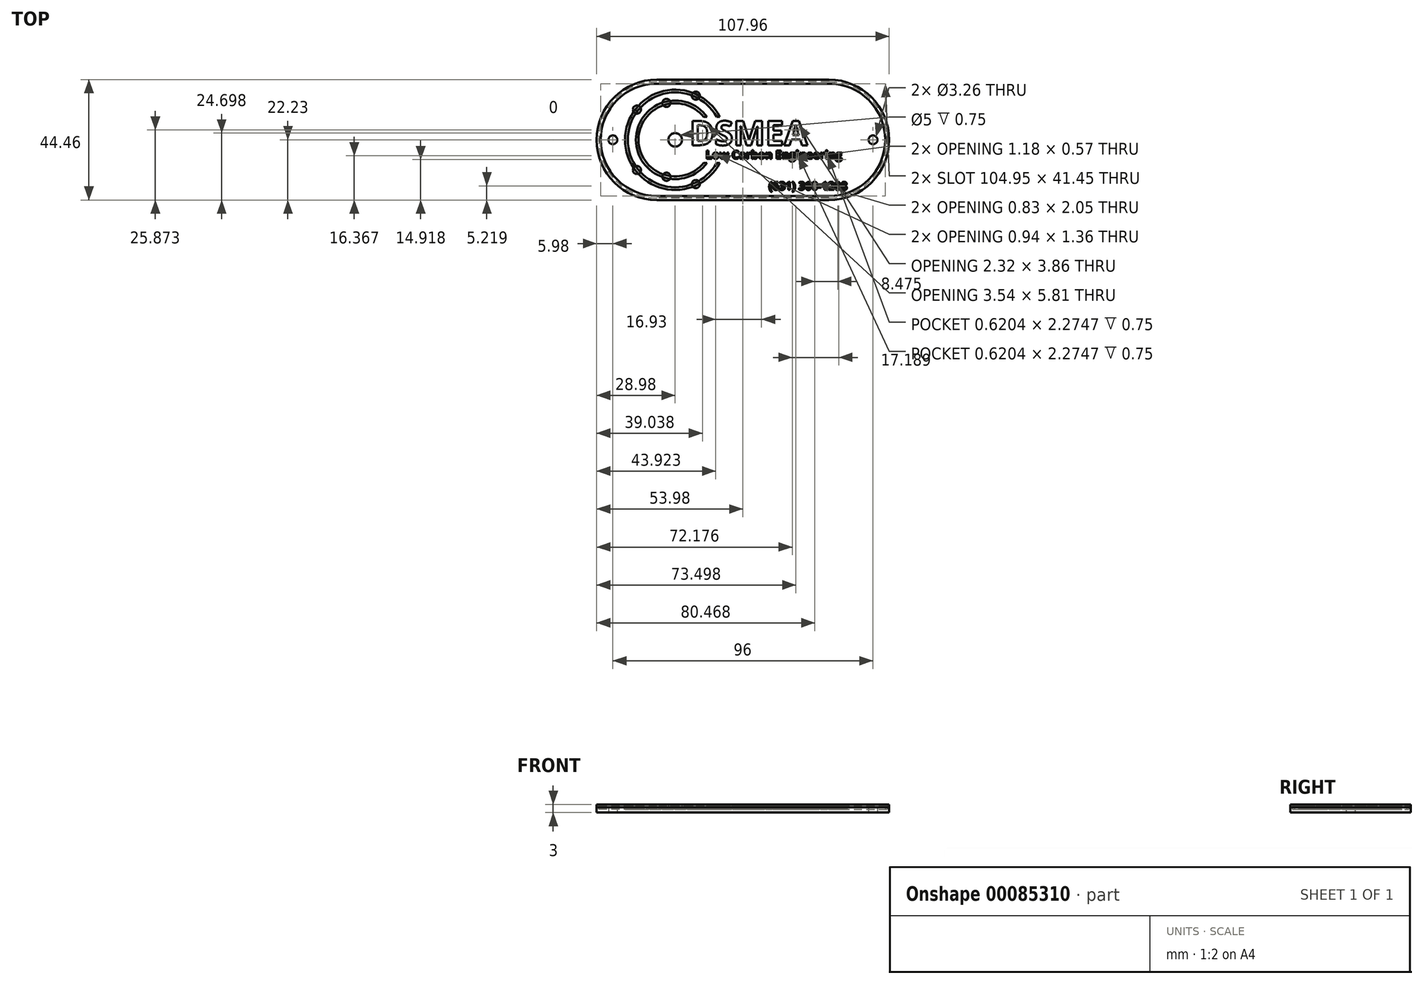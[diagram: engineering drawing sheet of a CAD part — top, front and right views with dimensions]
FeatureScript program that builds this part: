
annotation { "Feature Type Name" : "Feature", "Feature Type Description" : "" }
export const myFeature = defineFeature(function(context is Context, id is Id, definition is map)
    precondition{}
    {
        {
            var Q0;
            Q0=qCreatedBy(makeId("Top.planeOp"),FACE);
            var sketch = newSketch(context, id + "F0", { "sketchPlane" : qUnion([Q0])});
            skLineSegment(sketch, "E0.bottom", {"start": v(31.75, 22.22) * mm, "end": v(-31.75, 22.22) * mm});
            skLineSegment(sketch, "E0.top", {"start": v(31.75, -22.23) * mm, "end": v(-31.75, -22.23) * mm});
            skPoint(sketch, "E0.middle", {"position": v(0, 0) * mm});
            skArc(sketch, "E1", {"start": v(31.75, -22.23) * mm, "mid": v(53.98, 0) * mm, "end": v(31.75, 22.23) * mm});
            skArc(sketch, "E2", {"start": v(-31.75, 22.23) * mm, "mid": v(-53.98, 0) * mm, "end": v(-31.75, -22.23) * mm});
            skSolve(sketch);
        }
        {
            var Q0;
            Q0 = qSketchRegion(id + "F0", true);
            extrude(context, id + "F1", {"entities" : qUnion([Q0]), "depth" : 2 * mm});
        }
        {
            var Q0;
            Q0=qCreatedBy(makeId("Top.planeOp"),FACE);
            cPlane(context, id + "F2", {"entities" : qUnion([Q0]), "cplaneType" : CPlaneType.OFFSET, "offset" : 1.25 * mm, "width" : 150 * mm, "height" : 150 * mm});
        }
        {
            var Q0;
            Q0=qCreatedBy(id+"F2.planeOp",FACE);
            var sketch = newSketch(context, id + "F3", { "sketchPlane" : qUnion([Q0])});
            skPoint(sketch, "E3.middle", {"position": v(0, 0) * mm});
            skLineSegment(sketch, "E4.0", {"start": v(31.75, 20.73) * mm, "end": v(-31.75, 20.73) * mm});
            skArc(sketch, "E5.0", {"start": v(31.75, -20.73) * mm, "mid": v(52.48, 0) * mm, "end": v(31.75, 20.73) * mm});
            skLineSegment(sketch, "E6.0", {"start": v(31.75, -20.73) * mm, "end": v(-31.75, -20.73) * mm});
            skArc(sketch, "E7.0", {"start": v(-31.75, 20.73) * mm, "mid": v(-52.48, 0) * mm, "end": v(-31.75, -20.73) * mm});
            skLineSegment(sketch, "E8.0", {"start": v(31.75, 21.48) * mm, "end": v(-31.75, 21.48) * mm});
            skArc(sketch, "E9.0", {"start": v(-31.75, 21.48) * mm, "mid": v(-53.23, 0) * mm, "end": v(-31.75, -21.48) * mm});
            skArc(sketch, "E10.0", {"start": v(31.75, -21.48) * mm, "mid": v(53.23, 0) * mm, "end": v(31.75, 21.48) * mm});
            skLineSegment(sketch, "E11.0", {"start": v(31.75, -21.48) * mm, "end": v(-31.75, -21.48) * mm});
            skSolve(sketch);
        }
        {
            var Q0;
            Q0 = qSketchRegion(id + "F3", true);
            extrude(context, id + "F4", {"entities" : qUnion([Q0]), "depth" : 1.25 * mm});
        }
        {
            var Q0;
            {var subQ0=sQuery(id+"F0.wireOp",EDGE,"E0.bottom");var subQ1=makeQuery(id+"F1.opExtrude","SWEPT_FACE",FACE,{"disambiguationData":[OSD([subQ0])]});var subQ3=sQuery(id+"F0.wireOp",EDGE,"E0.top");var subQ5=sQuery(id+"F0.wireOp",EDGE,"E1");var subQ7=sQuery(id+"F0.wireOp",EDGE,"E2");Q0=makeQuery(id+"F14.boolean.opBoolean","SPLIT",FACE,{"disambiguationData":[TD([subQ1])],"derivedFrom":makeQuery(id+"F8.boolean.opBoolean","SPLIT",FACE,{"disambiguationData":[TD([subQ1])],"derivedFrom":makeQuery(id+"F1.opExtrude","CAP_FACE",FACE,{"disambiguationData":[OSD([subQ0,subQ3,subQ5,subQ7])],"isStart":false})})});}
            var sketch = newSketch(context, id + "F5", { "sketchPlane" : qUnion([Q0])});
            skArc(sketch, "E12", {"start": v(-31.75, 22.23) * mm, "mid": v(-53.98, 0) * mm, "end": v(-31.75, -22.23) * mm});
            skArc(sketch, "E13.0", {"start": v(-31.75, 20.73) * mm, "mid": v(-52.48, 0) * mm, "end": v(-31.75, -20.73) * mm});
            skArc(sketch, "E14.MirrorC", {"start": v(31.75, 22.23) * mm, "mid": v(53.98, 0) * mm, "end": v(31.75, -22.23) * mm});
            skArc(sketch, "E15.MirrorC", {"start": v(31.75, 20.73) * mm, "mid": v(52.48, 0) * mm, "end": v(31.75, -20.73) * mm});
            skLineSegment(sketch, "E16", {"start": v(-31.75, -22.23) * mm, "end": v(31.75, -22.23) * mm});
            skLineSegment(sketch, "E17.MirrorCS", {"start": v(-31.75, 22.23) * mm, "end": v(31.75, 22.23) * mm});
            skLineSegment(sketch, "E18.0", {"start": v(-31.75, 20.73) * mm, "end": v(31.75, 20.73) * mm});
            skLineSegment(sketch, "E19.MirrorCS", {"start": v(-31.75, -20.73) * mm, "end": v(31.75, -20.73) * mm});
            skSolve(sketch);
        }
        {
            var Q0;
            Q0 = qSketchRegion(id + "F5", true);
            extrude(context, id + "F6", {"entities" : qUnion([Q0]), "depth" : 1 * mm});
        }
        {
            var Q0;
            Q0=qCreatedBy(id+"F2.planeOp",FACE);
            var sketch = newSketch(context, id + "F7", { "sketchPlane" : qUnion([Q0])});
            skArc(sketch, "E20", {"start": v(-8.57, 8.5) * mm, "mid": v(-43.5, 0) * mm, "end": v(-8.57, -8.5) * mm});
            skArc(sketch, "E21", {"start": v(-9.7, 8.5) * mm, "mid": v(-42.5, 0) * mm, "end": v(-9.7, -8.5) * mm});
            skLineSegment(sketch, "E22.bottom", {"start": v(-8.57, 8.5) * mm, "end": v(-9.7, 8.5) * mm});
            skLineSegment(sketch, "E22.top", {"start": v(-8.57, -8.5) * mm, "end": v(-9.7, -8.5) * mm});
            skPoint(sketch, "E22.middle", {"position": v(0, 0) * mm});
            skSolve(sketch);
        }
        {
            var Q0;
            Q0 = qSketchRegion(id + "F7", true);
            extrude(context, id + "F8", {"entities" : qUnion([Q0]), "depth" : 1.75 * mm});
        }
        {
            var Q0;
            Q0=qCreatedBy(id+"F2.planeOp",FACE);
            var sketch = newSketch(context, id + "F9", { "sketchPlane" : qUnion([Q0])});
            skArc(sketch, "E23", {"start": v(-13.25, 8.5) * mm, "mid": v(-39.5, 0) * mm, "end": v(-13.25, -8.5) * mm});
            skArc(sketch, "E24", {"start": v(-14.51, 8.5) * mm, "mid": v(-38.5, 0) * mm, "end": v(-14.51, -8.5) * mm});
            skLineSegment(sketch, "E25.bottom", {"start": v(-13.25, 8.5) * mm, "end": v(-14.51, 8.5) * mm});
            skLineSegment(sketch, "E25.top", {"start": v(-13.25, -8.5) * mm, "end": v(-14.51, -8.5) * mm});
            skPoint(sketch, "E25.middle", {"position": v(0, 0) * mm});
            skSolve(sketch);
        }
        {
            var Q0;
            Q0 = qSketchRegion(id + "F9", true);
            extrude(context, id + "F10", {"entities" : qUnion([Q0]), "depth" : 1.75 * mm});
        }
        {
            var Q0;
            Q0=qCreatedBy(id+"F2.planeOp",FACE);
            var sketch = newSketch(context, id + "F11", { "sketchPlane" : qUnion([Q0])});
            skCircle(sketch, "E26", {"center": v(-25, 0) * mm, "radius": 2.5 * mm});
            skCircle(sketch, "E27", {"center": v(-17.4, 16.31) * mm, "radius": 1.5 * mm});
            skLineSegment(sketch, "E28.anchor1", {"start": v(-25, 0) * mm, "end": v(-17.4, 16.31) * mm, "construction": true});
            skLineSegment(sketch, "E28.anchor2", {"start": v(-25, 0) * mm, "end": v(-17.4, -16.31) * mm, "construction": true});
            skCircle(sketch, "E29", {"center": v(-28.23, 13.62) * mm, "radius": 1.5 * mm});
            skCircle(sketch, "E30.MirrorC", {"center": v(-28.23, -13.62) * mm, "radius": 1.5 * mm});
            skLineSegment(sketch, "E31", {"start": v(-59.58, 0) * mm, "end": v(0, 0) * mm, "construction": true});
            skCircle(sketch, "E32", {"center": v(-25, 0) * mm, "radius": 18 * mm, "construction": true});
            skCircle(sketch, "E33", {"center": v(-25, 0) * mm, "radius": 14 * mm, "construction": true});
            skLineSegment(sketch, "E34", {"start": v(-28.23, 13.62) * mm, "end": v(-35.98, 8.68) * mm, "construction": true});
            skLineSegment(sketch, "E35", {"start": v(-28.23, 13.62) * mm, "end": v(-19.08, 12.69) * mm, "construction": true});
            skCircle(sketch, "E36.1.0", {"center": v(-39.12, 11.16) * mm, "radius": 1.5 * mm});
            skCircle(sketch, "E36.2.0", {"center": v(-39.12, -11.16) * mm, "radius": 1.5 * mm});
            skCircle(sketch, "E36.3.0", {"center": v(-17.4, -16.31) * mm, "radius": 1.5 * mm});
            skSolve(sketch);
        }
        {
            var Q0;
            Q0 = qSketchRegion(id + "F11", true);
            extrude(context, id + "F12", {"entities" : qUnion([Q0]), "depth" : 1.75 * mm});
        }
        {
            var Q0;
            Q0=qCreatedBy(id+"F2.planeOp",FACE);
            var sketch = newSketch(context, id + "F13", { "sketchPlane" : qUnion([Q0])});
            skText(sketch, "E37", { "text": "DSMEA", "fontName": "OpenSans-Bold.ttf"});
            const initialGuessF13  = {"E37": [-0.01973, -0.002, 1, 0, 0.009]};
            skSetInitialGuess(sketch, initialGuessF13);
            skSolve(sketch);
        }
        {
            var Q0;
            Q0 = qSketchRegion(id + "F13", true);
            extrude(context, id + "F14", {"entities" : qUnion([Q0]), "depth" : 1.75 * mm});
        }
        {
            var Q0;
            Q0=qCreatedBy(id+"F2.planeOp",FACE);
            var sketch = newSketch(context, id + "F15", { "sketchPlane" : qUnion([Q0])});
            skText(sketch, "E38", { "text": "Low Carbon Engineering", "fontName": "OpenSans-Bold.ttf"});
            const initialGuessF15  = {"E38": [-0.0137, -0.007, 1, 0, 0.003]};
            skSetInitialGuess(sketch, initialGuessF15);
            skSolve(sketch);
        }
        {
            var Q0;
            Q0 = qSketchRegion(id + "F15", true);
            extrude(context, id + "F16", {"entities" : qUnion([Q0]), "depth" : 1.75 * mm});
        }
        {
            var Q0;
            Q0=qCreatedBy(id+"F2.planeOp",FACE);
            var sketch = newSketch(context, id + "F17", { "sketchPlane" : qUnion([Q0])});
            skText(sketch, "E39", { "text": "(631) 360-1208", "fontName": "OpenSans-Bold.ttf"});
            const initialGuessF17  = {"E39": [0.0095, -0.0185, 1, 0, 0.003]};
            skSetInitialGuess(sketch, initialGuessF17);
            skSolve(sketch);
        }
        {
            var Q0;
            Q0 = qSketchRegion(id + "F17", true);
            extrude(context, id + "F18", {"entities" : qUnion([Q0]), "depth" : 1.75 * mm});
        }
        {
            var Q0;
            Q0=makeQuery(id+"F4.opExtrude","SWEPT_BODY",BODY,{"disambiguationData":[OSD([sQuery(id+"F3.wireOp",EDGE,"E4.0"),sQuery(id+"F3.wireOp",EDGE,"E5.0"),sQuery(id+"F3.wireOp",EDGE,"E6.0"),sQuery(id+"F3.wireOp",EDGE,"E7.0"),sQuery(id+"F3.wireOp",EDGE,"E8.0"),sQuery(id+"F3.wireOp",EDGE,"E9.0"),sQuery(id+"F3.wireOp",EDGE,"E10.0"),sQuery(id+"F3.wireOp",EDGE,"E11.0")])]});
            var Q1;
            Q1=makeQuery(id+"F1.opExtrude","SWEPT_BODY",BODY,{"disambiguationData":[OSD([sQuery(id+"F0.wireOp",EDGE,"E0.bottom"),sQuery(id+"F0.wireOp",EDGE,"E0.top"),sQuery(id+"F0.wireOp",EDGE,"E1"),sQuery(id+"F0.wireOp",EDGE,"E2")])]});
            booleanBodies(context, id + "F19", {"operationType" : BooleanOperationType.SUBTRACTION, "tools" : qUnion([Q0]), "targets" : qUnion([Q1]), "keepTools" : true});
        }
        {
            var Q0;
            Q0=makeQuery(id+"F8.opExtrude","SWEPT_BODY",BODY,{"disambiguationData":[OSD([sQuery(id+"F7.wireOp",EDGE,"E20"),sQuery(id+"F7.wireOp",EDGE,"E21")])]});
            var Q1;
            Q1=makeQuery(id+"F1.opExtrude","SWEPT_BODY",BODY,{"disambiguationData":[OSD([sQuery(id+"F0.wireOp",EDGE,"E0.bottom"),sQuery(id+"F0.wireOp",EDGE,"E0.top"),sQuery(id+"F0.wireOp",EDGE,"E1"),sQuery(id+"F0.wireOp",EDGE,"E2")])]});
            booleanBodies(context, id + "F20", {"operationType" : BooleanOperationType.SUBTRACTION, "tools" : qUnion([Q0]), "targets" : qUnion([Q1]), "keepTools" : true});
        }
        {
            var Q0;
            Q0=makeQuery(id+"F8.opExtrude","SWEPT_BODY",BODY,{"disambiguationData":[OSD([sQuery(id+"F7.wireOp",EDGE,"E20"),sQuery(id+"F7.wireOp",EDGE,"E21")])]});
            var Q1;
            Q1=makeQuery(id+"F12.opExtrude","SWEPT_BODY",BODY,{"disambiguationData":[OSD([sQuery(id+"F11.wireOp",EDGE,"E26")])]});
            var Q2;
            Q2=makeQuery(id+"F10.opExtrude","SWEPT_BODY",BODY,{"disambiguationData":[OSD([sQuery(id+"F9.wireOp",EDGE,"E23"),sQuery(id+"F9.wireOp",EDGE,"E24")])]});
            var Q3;
            Q3=makeQuery(id+"F1.opExtrude","SWEPT_BODY",BODY,{"disambiguationData":[OSD([sQuery(id+"F0.wireOp",EDGE,"E0.bottom"),sQuery(id+"F0.wireOp",EDGE,"E0.top"),sQuery(id+"F0.wireOp",EDGE,"E1"),sQuery(id+"F0.wireOp",EDGE,"E2")])]});
            booleanBodies(context, id + "F21", {"operationType" : BooleanOperationType.SUBTRACTION, "tools" : qUnion([Q0, Q1, Q2]), "targets" : qUnion([Q3]), "keepTools" : true});
        }
        {
            var Q0;
            Q0=makeQuery(id+"F14.opExtrude","SWEPT_BODY",BODY,{"disambiguationData":[OSD([sQuery(id+"F13.wireOp",EDGE,"E37.sketch_text.stroke-0"),sQuery(id+"F13.wireOp",EDGE,"E37.sketch_text.stroke-1"),sQuery(id+"F13.wireOp",EDGE,"E37.sketch_text.stroke-2"),sQuery(id+"F13.wireOp",EDGE,"E37.sketch_text.stroke-3"),sQuery(id+"F13.wireOp",EDGE,"E37.sketch_text.stroke-4"),sQuery(id+"F13.wireOp",EDGE,"E37.sketch_text.stroke-5"),sQuery(id+"F13.wireOp",EDGE,"E37.sketch_text.stroke-6"),sQuery(id+"F13.wireOp",EDGE,"E37.sketch_text.stroke-7"),sQuery(id+"F13.wireOp",EDGE,"E37.sketch_text.stroke-8"),sQuery(id+"F13.wireOp",EDGE,"E37.sketch_text.stroke-9"),sQuery(id+"F13.wireOp",EDGE,"E37.sketch_text.stroke-10"),sQuery(id+"F13.wireOp",EDGE,"E37.sketch_text.stroke-11")])]});
            var Q1;
            Q1=makeQuery(id+"F14.opExtrude","SWEPT_BODY",BODY,{"disambiguationData":[OSD([sQuery(id+"F13.wireOp",EDGE,"E37.sketch_text.stroke-12"),sQuery(id+"F13.wireOp",EDGE,"E37.sketch_text.stroke-13"),sQuery(id+"F13.wireOp",EDGE,"E37.sketch_text.stroke-14"),sQuery(id+"F13.wireOp",EDGE,"E37.sketch_text.stroke-15"),sQuery(id+"F13.wireOp",EDGE,"E37.sketch_text.stroke-16"),sQuery(id+"F13.wireOp",EDGE,"E37.sketch_text.stroke-17"),sQuery(id+"F13.wireOp",EDGE,"E37.sketch_text.stroke-18"),sQuery(id+"F13.wireOp",EDGE,"E37.sketch_text.stroke-19"),sQuery(id+"F13.wireOp",EDGE,"E37.sketch_text.stroke-20"),sQuery(id+"F13.wireOp",EDGE,"E37.sketch_text.stroke-21"),sQuery(id+"F13.wireOp",EDGE,"E37.sketch_text.stroke-22"),sQuery(id+"F13.wireOp",EDGE,"E37.sketch_text.stroke-23"),sQuery(id+"F13.wireOp",EDGE,"E37.sketch_text.stroke-24"),sQuery(id+"F13.wireOp",EDGE,"E37.sketch_text.stroke-25"),sQuery(id+"F13.wireOp",EDGE,"E37.sketch_text.stroke-26"),sQuery(id+"F13.wireOp",EDGE,"E37.sketch_text.stroke-27"),sQuery(id+"F13.wireOp",EDGE,"E37.sketch_text.stroke-28"),sQuery(id+"F13.wireOp",EDGE,"E37.sketch_text.stroke-29"),sQuery(id+"F13.wireOp",EDGE,"E37.sketch_text.stroke-30"),sQuery(id+"F13.wireOp",EDGE,"E37.sketch_text.stroke-31"),sQuery(id+"F13.wireOp",EDGE,"E37.sketch_text.stroke-32"),sQuery(id+"F13.wireOp",EDGE,"E37.sketch_text.stroke-33"),sQuery(id+"F13.wireOp",EDGE,"E37.sketch_text.stroke-34"),sQuery(id+"F13.wireOp",EDGE,"E37.sketch_text.stroke-35"),sQuery(id+"F13.wireOp",EDGE,"E37.sketch_text.stroke-36"),sQuery(id+"F13.wireOp",EDGE,"E37.sketch_text.stroke-37"),sQuery(id+"F13.wireOp",EDGE,"E37.sketch_text.stroke-38"),sQuery(id+"F13.wireOp",EDGE,"E37.sketch_text.stroke-39")])]});
            var Q2;
            Q2=makeQuery(id+"F14.opExtrude","SWEPT_BODY",BODY,{"disambiguationData":[OSD([sQuery(id+"F13.wireOp",EDGE,"E37.sketch_text.stroke-40"),sQuery(id+"F13.wireOp",EDGE,"E37.sketch_text.stroke-41"),sQuery(id+"F13.wireOp",EDGE,"E37.sketch_text.stroke-42"),sQuery(id+"F13.wireOp",EDGE,"E37.sketch_text.stroke-43"),sQuery(id+"F13.wireOp",EDGE,"E37.sketch_text.stroke-44"),sQuery(id+"F13.wireOp",EDGE,"E37.sketch_text.stroke-45"),sQuery(id+"F13.wireOp",EDGE,"E37.sketch_text.stroke-46"),sQuery(id+"F13.wireOp",EDGE,"E37.sketch_text.stroke-47"),sQuery(id+"F13.wireOp",EDGE,"E37.sketch_text.stroke-48"),sQuery(id+"F13.wireOp",EDGE,"E37.sketch_text.stroke-49"),sQuery(id+"F13.wireOp",EDGE,"E37.sketch_text.stroke-50"),sQuery(id+"F13.wireOp",EDGE,"E37.sketch_text.stroke-51"),sQuery(id+"F13.wireOp",EDGE,"E37.sketch_text.stroke-52"),sQuery(id+"F13.wireOp",EDGE,"E37.sketch_text.stroke-53"),sQuery(id+"F13.wireOp",EDGE,"E37.sketch_text.stroke-54"),sQuery(id+"F13.wireOp",EDGE,"E37.sketch_text.stroke-55"),sQuery(id+"F13.wireOp",EDGE,"E37.sketch_text.stroke-56"),sQuery(id+"F13.wireOp",EDGE,"E37.sketch_text.stroke-57"),sQuery(id+"F13.wireOp",EDGE,"E37.sketch_text.stroke-58")])]});
            var Q3;
            Q3=makeQuery(id+"F14.opExtrude","SWEPT_BODY",BODY,{"disambiguationData":[OSD([sQuery(id+"F13.wireOp",EDGE,"E37.sketch_text.stroke-59"),sQuery(id+"F13.wireOp",EDGE,"E37.sketch_text.stroke-60"),sQuery(id+"F13.wireOp",EDGE,"E37.sketch_text.stroke-61"),sQuery(id+"F13.wireOp",EDGE,"E37.sketch_text.stroke-62"),sQuery(id+"F13.wireOp",EDGE,"E37.sketch_text.stroke-63"),sQuery(id+"F13.wireOp",EDGE,"E37.sketch_text.stroke-64"),sQuery(id+"F13.wireOp",EDGE,"E37.sketch_text.stroke-65"),sQuery(id+"F13.wireOp",EDGE,"E37.sketch_text.stroke-66"),sQuery(id+"F13.wireOp",EDGE,"E37.sketch_text.stroke-67"),sQuery(id+"F13.wireOp",EDGE,"E37.sketch_text.stroke-68"),sQuery(id+"F13.wireOp",EDGE,"E37.sketch_text.stroke-69"),sQuery(id+"F13.wireOp",EDGE,"E37.sketch_text.stroke-70")])]});
            var Q4;
            Q4=makeQuery(id+"F14.opExtrude","SWEPT_BODY",BODY,{"disambiguationData":[OSD([sQuery(id+"F13.wireOp",EDGE,"E37.sketch_text.stroke-71"),sQuery(id+"F13.wireOp",EDGE,"E37.sketch_text.stroke-72"),sQuery(id+"F13.wireOp",EDGE,"E37.sketch_text.stroke-73"),sQuery(id+"F13.wireOp",EDGE,"E37.sketch_text.stroke-74"),sQuery(id+"F13.wireOp",EDGE,"E37.sketch_text.stroke-75"),sQuery(id+"F13.wireOp",EDGE,"E37.sketch_text.stroke-76"),sQuery(id+"F13.wireOp",EDGE,"E37.sketch_text.stroke-77"),sQuery(id+"F13.wireOp",EDGE,"E37.sketch_text.stroke-78"),sQuery(id+"F13.wireOp",EDGE,"E37.sketch_text.stroke-79"),sQuery(id+"F13.wireOp",EDGE,"E37.sketch_text.stroke-80"),sQuery(id+"F13.wireOp",EDGE,"E37.sketch_text.stroke-81"),sQuery(id+"F13.wireOp",EDGE,"E37.sketch_text.stroke-82")])]});
            var Q5;
            Q5=makeQuery(id+"F1.opExtrude","SWEPT_BODY",BODY,{"disambiguationData":[OSD([sQuery(id+"F0.wireOp",EDGE,"E0.bottom"),sQuery(id+"F0.wireOp",EDGE,"E0.top"),sQuery(id+"F0.wireOp",EDGE,"E1"),sQuery(id+"F0.wireOp",EDGE,"E2")])]});
            booleanBodies(context, id + "F22", {"operationType" : BooleanOperationType.SUBTRACTION, "tools" : qUnion([Q0, Q1, Q2, Q3, Q4]), "targets" : qUnion([Q5]), "keepTools" : true});
        }
        {
            var Q0;
            Q0=makeQuery(id+"F16.opExtrude","SWEPT_BODY",BODY,{"disambiguationData":[OSD([sQuery(id+"F15.wireOp",EDGE,"E38.sketch_text.stroke-0"),sQuery(id+"F15.wireOp",EDGE,"E38.sketch_text.stroke-1"),sQuery(id+"F15.wireOp",EDGE,"E38.sketch_text.stroke-2"),sQuery(id+"F15.wireOp",EDGE,"E38.sketch_text.stroke-3"),sQuery(id+"F15.wireOp",EDGE,"E38.sketch_text.stroke-4"),sQuery(id+"F15.wireOp",EDGE,"E38.sketch_text.stroke-5")])]});
            var Q1;
            Q1=makeQuery(id+"F16.opExtrude","SWEPT_BODY",BODY,{"disambiguationData":[OSD([sQuery(id+"F15.wireOp",EDGE,"E38.sketch_text.stroke-6"),sQuery(id+"F15.wireOp",EDGE,"E38.sketch_text.stroke-7"),sQuery(id+"F15.wireOp",EDGE,"E38.sketch_text.stroke-8"),sQuery(id+"F15.wireOp",EDGE,"E38.sketch_text.stroke-9"),sQuery(id+"F15.wireOp",EDGE,"E38.sketch_text.stroke-10"),sQuery(id+"F15.wireOp",EDGE,"E38.sketch_text.stroke-11"),sQuery(id+"F15.wireOp",EDGE,"E38.sketch_text.stroke-12"),sQuery(id+"F15.wireOp",EDGE,"E38.sketch_text.stroke-13"),sQuery(id+"F15.wireOp",EDGE,"E38.sketch_text.stroke-14"),sQuery(id+"F15.wireOp",EDGE,"E38.sketch_text.stroke-15"),sQuery(id+"F15.wireOp",EDGE,"E38.sketch_text.stroke-16"),sQuery(id+"F15.wireOp",EDGE,"E38.sketch_text.stroke-17"),sQuery(id+"F15.wireOp",EDGE,"E38.sketch_text.stroke-18"),sQuery(id+"F15.wireOp",EDGE,"E38.sketch_text.stroke-19"),sQuery(id+"F15.wireOp",EDGE,"E38.sketch_text.stroke-20"),sQuery(id+"F15.wireOp",EDGE,"E38.sketch_text.stroke-21"),sQuery(id+"F15.wireOp",EDGE,"E38.sketch_text.stroke-22"),sQuery(id+"F15.wireOp",EDGE,"E38.sketch_text.stroke-23")])]});
            var Q2;
            Q2=makeQuery(id+"F16.opExtrude","SWEPT_BODY",BODY,{"disambiguationData":[OSD([sQuery(id+"F15.wireOp",EDGE,"E38.sketch_text.stroke-24"),sQuery(id+"F15.wireOp",EDGE,"E38.sketch_text.stroke-25"),sQuery(id+"F15.wireOp",EDGE,"E38.sketch_text.stroke-26"),sQuery(id+"F15.wireOp",EDGE,"E38.sketch_text.stroke-27"),sQuery(id+"F15.wireOp",EDGE,"E38.sketch_text.stroke-28"),sQuery(id+"F15.wireOp",EDGE,"E38.sketch_text.stroke-29"),sQuery(id+"F15.wireOp",EDGE,"E38.sketch_text.stroke-30"),sQuery(id+"F15.wireOp",EDGE,"E38.sketch_text.stroke-31"),sQuery(id+"F15.wireOp",EDGE,"E38.sketch_text.stroke-32"),sQuery(id+"F15.wireOp",EDGE,"E38.sketch_text.stroke-33"),sQuery(id+"F15.wireOp",EDGE,"E38.sketch_text.stroke-34"),sQuery(id+"F15.wireOp",EDGE,"E38.sketch_text.stroke-35"),sQuery(id+"F15.wireOp",EDGE,"E38.sketch_text.stroke-36"),sQuery(id+"F15.wireOp",EDGE,"E38.sketch_text.stroke-37"),sQuery(id+"F15.wireOp",EDGE,"E38.sketch_text.stroke-38"),sQuery(id+"F15.wireOp",EDGE,"E38.sketch_text.stroke-39"),sQuery(id+"F15.wireOp",EDGE,"E38.sketch_text.stroke-40"),sQuery(id+"F15.wireOp",EDGE,"E38.sketch_text.stroke-41"),sQuery(id+"F15.wireOp",EDGE,"E38.sketch_text.stroke-42"),sQuery(id+"F15.wireOp",EDGE,"E38.sketch_text.stroke-43"),sQuery(id+"F15.wireOp",EDGE,"E38.sketch_text.stroke-44"),sQuery(id+"F15.wireOp",EDGE,"E38.sketch_text.stroke-45"),sQuery(id+"F15.wireOp",EDGE,"E38.sketch_text.stroke-46"),sQuery(id+"F15.wireOp",EDGE,"E38.sketch_text.stroke-47"),sQuery(id+"F15.wireOp",EDGE,"E38.sketch_text.stroke-48"),sQuery(id+"F15.wireOp",EDGE,"E38.sketch_text.stroke-49")])]});
            var Q3;
            Q3=makeQuery(id+"F16.opExtrude","SWEPT_BODY",BODY,{"disambiguationData":[OSD([sQuery(id+"F15.wireOp",EDGE,"E38.sketch_text.stroke-50"),sQuery(id+"F15.wireOp",EDGE,"E38.sketch_text.stroke-51"),sQuery(id+"F15.wireOp",EDGE,"E38.sketch_text.stroke-52"),sQuery(id+"F15.wireOp",EDGE,"E38.sketch_text.stroke-53"),sQuery(id+"F15.wireOp",EDGE,"E38.sketch_text.stroke-54"),sQuery(id+"F15.wireOp",EDGE,"E38.sketch_text.stroke-55"),sQuery(id+"F15.wireOp",EDGE,"E38.sketch_text.stroke-56"),sQuery(id+"F15.wireOp",EDGE,"E38.sketch_text.stroke-57"),sQuery(id+"F15.wireOp",EDGE,"E38.sketch_text.stroke-58"),sQuery(id+"F15.wireOp",EDGE,"E38.sketch_text.stroke-59"),sQuery(id+"F15.wireOp",EDGE,"E38.sketch_text.stroke-60"),sQuery(id+"F15.wireOp",EDGE,"E38.sketch_text.stroke-61"),sQuery(id+"F15.wireOp",EDGE,"E38.sketch_text.stroke-62"),sQuery(id+"F15.wireOp",EDGE,"E38.sketch_text.stroke-63"),sQuery(id+"F15.wireOp",EDGE,"E38.sketch_text.stroke-64")])]});
            var Q4;
            Q4=makeQuery(id+"F16.opExtrude","SWEPT_BODY",BODY,{"disambiguationData":[OSD([sQuery(id+"F15.wireOp",EDGE,"E38.sketch_text.stroke-65"),sQuery(id+"F15.wireOp",EDGE,"E38.sketch_text.stroke-66"),sQuery(id+"F15.wireOp",EDGE,"E38.sketch_text.stroke-67"),sQuery(id+"F15.wireOp",EDGE,"E38.sketch_text.stroke-68"),sQuery(id+"F15.wireOp",EDGE,"E38.sketch_text.stroke-69"),sQuery(id+"F15.wireOp",EDGE,"E38.sketch_text.stroke-70"),sQuery(id+"F15.wireOp",EDGE,"E38.sketch_text.stroke-71"),sQuery(id+"F15.wireOp",EDGE,"E38.sketch_text.stroke-72"),sQuery(id+"F15.wireOp",EDGE,"E38.sketch_text.stroke-73"),sQuery(id+"F15.wireOp",EDGE,"E38.sketch_text.stroke-74"),sQuery(id+"F15.wireOp",EDGE,"E38.sketch_text.stroke-75"),sQuery(id+"F15.wireOp",EDGE,"E38.sketch_text.stroke-76"),sQuery(id+"F15.wireOp",EDGE,"E38.sketch_text.stroke-77"),sQuery(id+"F15.wireOp",EDGE,"E38.sketch_text.stroke-78"),sQuery(id+"F15.wireOp",EDGE,"E38.sketch_text.stroke-79"),sQuery(id+"F15.wireOp",EDGE,"E38.sketch_text.stroke-80"),sQuery(id+"F15.wireOp",EDGE,"E38.sketch_text.stroke-81"),sQuery(id+"F15.wireOp",EDGE,"E38.sketch_text.stroke-82"),sQuery(id+"F15.wireOp",EDGE,"E38.sketch_text.stroke-83"),sQuery(id+"F15.wireOp",EDGE,"E38.sketch_text.stroke-84"),sQuery(id+"F15.wireOp",EDGE,"E38.sketch_text.stroke-85"),sQuery(id+"F15.wireOp",EDGE,"E38.sketch_text.stroke-86"),sQuery(id+"F15.wireOp",EDGE,"E38.sketch_text.stroke-87"),sQuery(id+"F15.wireOp",EDGE,"E38.sketch_text.stroke-88"),sQuery(id+"F15.wireOp",EDGE,"E38.sketch_text.stroke-89")])]});
            var Q5;
            Q5=makeQuery(id+"F16.opExtrude","SWEPT_BODY",BODY,{"disambiguationData":[OSD([sQuery(id+"F15.wireOp",EDGE,"E38.sketch_text.stroke-90"),sQuery(id+"F15.wireOp",EDGE,"E38.sketch_text.stroke-91"),sQuery(id+"F15.wireOp",EDGE,"E38.sketch_text.stroke-92"),sQuery(id+"F15.wireOp",EDGE,"E38.sketch_text.stroke-93"),sQuery(id+"F15.wireOp",EDGE,"E38.sketch_text.stroke-94"),sQuery(id+"F15.wireOp",EDGE,"E38.sketch_text.stroke-95"),sQuery(id+"F15.wireOp",EDGE,"E38.sketch_text.stroke-96"),sQuery(id+"F15.wireOp",EDGE,"E38.sketch_text.stroke-97"),sQuery(id+"F15.wireOp",EDGE,"E38.sketch_text.stroke-98"),sQuery(id+"F15.wireOp",EDGE,"E38.sketch_text.stroke-99"),sQuery(id+"F15.wireOp",EDGE,"E38.sketch_text.stroke-100"),sQuery(id+"F15.wireOp",EDGE,"E38.sketch_text.stroke-101"),sQuery(id+"F15.wireOp",EDGE,"E38.sketch_text.stroke-102")])]});
            var Q6;
            Q6=makeQuery(id+"F16.opExtrude","SWEPT_BODY",BODY,{"disambiguationData":[OSD([sQuery(id+"F15.wireOp",EDGE,"E38.sketch_text.stroke-103"),sQuery(id+"F15.wireOp",EDGE,"E38.sketch_text.stroke-104"),sQuery(id+"F15.wireOp",EDGE,"E38.sketch_text.stroke-105"),sQuery(id+"F15.wireOp",EDGE,"E38.sketch_text.stroke-106"),sQuery(id+"F15.wireOp",EDGE,"E38.sketch_text.stroke-107"),sQuery(id+"F15.wireOp",EDGE,"E38.sketch_text.stroke-108"),sQuery(id+"F15.wireOp",EDGE,"E38.sketch_text.stroke-109"),sQuery(id+"F15.wireOp",EDGE,"E38.sketch_text.stroke-110"),sQuery(id+"F15.wireOp",EDGE,"E38.sketch_text.stroke-111"),sQuery(id+"F15.wireOp",EDGE,"E38.sketch_text.stroke-112"),sQuery(id+"F15.wireOp",EDGE,"E38.sketch_text.stroke-113"),sQuery(id+"F15.wireOp",EDGE,"E38.sketch_text.stroke-114"),sQuery(id+"F15.wireOp",EDGE,"E38.sketch_text.stroke-115"),sQuery(id+"F15.wireOp",EDGE,"E38.sketch_text.stroke-116"),sQuery(id+"F15.wireOp",EDGE,"E38.sketch_text.stroke-117"),sQuery(id+"F15.wireOp",EDGE,"E38.sketch_text.stroke-118"),sQuery(id+"F15.wireOp",EDGE,"E38.sketch_text.stroke-119"),sQuery(id+"F15.wireOp",EDGE,"E38.sketch_text.stroke-120"),sQuery(id+"F15.wireOp",EDGE,"E38.sketch_text.stroke-121"),sQuery(id+"F15.wireOp",EDGE,"E38.sketch_text.stroke-122"),sQuery(id+"F15.wireOp",EDGE,"E38.sketch_text.stroke-123"),sQuery(id+"F15.wireOp",EDGE,"E38.sketch_text.stroke-124"),sQuery(id+"F15.wireOp",EDGE,"E38.sketch_text.stroke-125")])]});
            var Q7;
            Q7=makeQuery(id+"F16.opExtrude","SWEPT_BODY",BODY,{"disambiguationData":[OSD([sQuery(id+"F15.wireOp",EDGE,"E38.sketch_text.stroke-126"),sQuery(id+"F15.wireOp",EDGE,"E38.sketch_text.stroke-127"),sQuery(id+"F15.wireOp",EDGE,"E38.sketch_text.stroke-128"),sQuery(id+"F15.wireOp",EDGE,"E38.sketch_text.stroke-129"),sQuery(id+"F15.wireOp",EDGE,"E38.sketch_text.stroke-130"),sQuery(id+"F15.wireOp",EDGE,"E38.sketch_text.stroke-131"),sQuery(id+"F15.wireOp",EDGE,"E38.sketch_text.stroke-132"),sQuery(id+"F15.wireOp",EDGE,"E38.sketch_text.stroke-133"),sQuery(id+"F15.wireOp",EDGE,"E38.sketch_text.stroke-134"),sQuery(id+"F15.wireOp",EDGE,"E38.sketch_text.stroke-135"),sQuery(id+"F15.wireOp",EDGE,"E38.sketch_text.stroke-136"),sQuery(id+"F15.wireOp",EDGE,"E38.sketch_text.stroke-137"),sQuery(id+"F15.wireOp",EDGE,"E38.sketch_text.stroke-138"),sQuery(id+"F15.wireOp",EDGE,"E38.sketch_text.stroke-139"),sQuery(id+"F15.wireOp",EDGE,"E38.sketch_text.stroke-140"),sQuery(id+"F15.wireOp",EDGE,"E38.sketch_text.stroke-141"),sQuery(id+"F15.wireOp",EDGE,"E38.sketch_text.stroke-142"),sQuery(id+"F15.wireOp",EDGE,"E38.sketch_text.stroke-143")])]});
            var Q8;
            Q8=makeQuery(id+"F16.opExtrude","SWEPT_BODY",BODY,{"disambiguationData":[OSD([sQuery(id+"F15.wireOp",EDGE,"E38.sketch_text.stroke-144"),sQuery(id+"F15.wireOp",EDGE,"E38.sketch_text.stroke-145"),sQuery(id+"F15.wireOp",EDGE,"E38.sketch_text.stroke-146"),sQuery(id+"F15.wireOp",EDGE,"E38.sketch_text.stroke-147"),sQuery(id+"F15.wireOp",EDGE,"E38.sketch_text.stroke-148"),sQuery(id+"F15.wireOp",EDGE,"E38.sketch_text.stroke-149"),sQuery(id+"F15.wireOp",EDGE,"E38.sketch_text.stroke-150"),sQuery(id+"F15.wireOp",EDGE,"E38.sketch_text.stroke-151"),sQuery(id+"F15.wireOp",EDGE,"E38.sketch_text.stroke-152"),sQuery(id+"F15.wireOp",EDGE,"E38.sketch_text.stroke-153"),sQuery(id+"F15.wireOp",EDGE,"E38.sketch_text.stroke-154"),sQuery(id+"F15.wireOp",EDGE,"E38.sketch_text.stroke-155"),sQuery(id+"F15.wireOp",EDGE,"E38.sketch_text.stroke-156"),sQuery(id+"F15.wireOp",EDGE,"E38.sketch_text.stroke-157"),sQuery(id+"F15.wireOp",EDGE,"E38.sketch_text.stroke-158"),sQuery(id+"F15.wireOp",EDGE,"E38.sketch_text.stroke-159"),sQuery(id+"F15.wireOp",EDGE,"E38.sketch_text.stroke-160")])]});
            var Q9;
            Q9=makeQuery(id+"F16.opExtrude","SWEPT_BODY",BODY,{"disambiguationData":[OSD([sQuery(id+"F15.wireOp",EDGE,"E38.sketch_text.stroke-161"),sQuery(id+"F15.wireOp",EDGE,"E38.sketch_text.stroke-162"),sQuery(id+"F15.wireOp",EDGE,"E38.sketch_text.stroke-163"),sQuery(id+"F15.wireOp",EDGE,"E38.sketch_text.stroke-164"),sQuery(id+"F15.wireOp",EDGE,"E38.sketch_text.stroke-165"),sQuery(id+"F15.wireOp",EDGE,"E38.sketch_text.stroke-166"),sQuery(id+"F15.wireOp",EDGE,"E38.sketch_text.stroke-167"),sQuery(id+"F15.wireOp",EDGE,"E38.sketch_text.stroke-168"),sQuery(id+"F15.wireOp",EDGE,"E38.sketch_text.stroke-169"),sQuery(id+"F15.wireOp",EDGE,"E38.sketch_text.stroke-170"),sQuery(id+"F15.wireOp",EDGE,"E38.sketch_text.stroke-171"),sQuery(id+"F15.wireOp",EDGE,"E38.sketch_text.stroke-172")])]});
            var Q10;
            Q10=makeQuery(id+"F16.opExtrude","SWEPT_BODY",BODY,{"disambiguationData":[OSD([sQuery(id+"F15.wireOp",EDGE,"E38.sketch_text.stroke-173"),sQuery(id+"F15.wireOp",EDGE,"E38.sketch_text.stroke-174"),sQuery(id+"F15.wireOp",EDGE,"E38.sketch_text.stroke-175"),sQuery(id+"F15.wireOp",EDGE,"E38.sketch_text.stroke-176"),sQuery(id+"F15.wireOp",EDGE,"E38.sketch_text.stroke-177"),sQuery(id+"F15.wireOp",EDGE,"E38.sketch_text.stroke-178"),sQuery(id+"F15.wireOp",EDGE,"E38.sketch_text.stroke-179"),sQuery(id+"F15.wireOp",EDGE,"E38.sketch_text.stroke-180"),sQuery(id+"F15.wireOp",EDGE,"E38.sketch_text.stroke-181"),sQuery(id+"F15.wireOp",EDGE,"E38.sketch_text.stroke-182"),sQuery(id+"F15.wireOp",EDGE,"E38.sketch_text.stroke-183"),sQuery(id+"F15.wireOp",EDGE,"E38.sketch_text.stroke-184"),sQuery(id+"F15.wireOp",EDGE,"E38.sketch_text.stroke-185"),sQuery(id+"F15.wireOp",EDGE,"E38.sketch_text.stroke-186"),sQuery(id+"F15.wireOp",EDGE,"E38.sketch_text.stroke-187"),sQuery(id+"F15.wireOp",EDGE,"E38.sketch_text.stroke-188"),sQuery(id+"F15.wireOp",EDGE,"E38.sketch_text.stroke-189")])]});
            var Q11;
            Q11=makeQuery(id+"F16.opExtrude","SWEPT_BODY",BODY,{"disambiguationData":[OSD([sQuery(id+"F15.wireOp",EDGE,"E38.sketch_text.stroke-190"),sQuery(id+"F15.wireOp",EDGE,"E38.sketch_text.stroke-191"),sQuery(id+"F15.wireOp",EDGE,"E38.sketch_text.stroke-192"),sQuery(id+"F15.wireOp",EDGE,"E38.sketch_text.stroke-193"),sQuery(id+"F15.wireOp",EDGE,"E38.sketch_text.stroke-194"),sQuery(id+"F15.wireOp",EDGE,"E38.sketch_text.stroke-195"),sQuery(id+"F15.wireOp",EDGE,"E38.sketch_text.stroke-196"),sQuery(id+"F15.wireOp",EDGE,"E38.sketch_text.stroke-197"),sQuery(id+"F15.wireOp",EDGE,"E38.sketch_text.stroke-198"),sQuery(id+"F15.wireOp",EDGE,"E38.sketch_text.stroke-199"),sQuery(id+"F15.wireOp",EDGE,"E38.sketch_text.stroke-200"),sQuery(id+"F15.wireOp",EDGE,"E38.sketch_text.stroke-201"),sQuery(id+"F15.wireOp",EDGE,"E38.sketch_text.stroke-202"),sQuery(id+"F15.wireOp",EDGE,"E38.sketch_text.stroke-203"),sQuery(id+"F15.wireOp",EDGE,"E38.sketch_text.stroke-204"),sQuery(id+"F15.wireOp",EDGE,"E38.sketch_text.stroke-205"),sQuery(id+"F15.wireOp",EDGE,"E38.sketch_text.stroke-206"),sQuery(id+"F15.wireOp",EDGE,"E38.sketch_text.stroke-207"),sQuery(id+"F15.wireOp",EDGE,"E38.sketch_text.stroke-208"),sQuery(id+"F15.wireOp",EDGE,"E38.sketch_text.stroke-209"),sQuery(id+"F15.wireOp",EDGE,"E38.sketch_text.stroke-210"),sQuery(id+"F15.wireOp",EDGE,"E38.sketch_text.stroke-211"),sQuery(id+"F15.wireOp",EDGE,"E38.sketch_text.stroke-212"),sQuery(id+"F15.wireOp",EDGE,"E38.sketch_text.stroke-213"),sQuery(id+"F15.wireOp",EDGE,"E38.sketch_text.stroke-214"),sQuery(id+"F15.wireOp",EDGE,"E38.sketch_text.stroke-215"),sQuery(id+"F15.wireOp",EDGE,"E38.sketch_text.stroke-216"),sQuery(id+"F15.wireOp",EDGE,"E38.sketch_text.stroke-217"),sQuery(id+"F15.wireOp",EDGE,"E38.sketch_text.stroke-218"),sQuery(id+"F15.wireOp",EDGE,"E38.sketch_text.stroke-219"),sQuery(id+"F15.wireOp",EDGE,"E38.sketch_text.stroke-220"),sQuery(id+"F15.wireOp",EDGE,"E38.sketch_text.stroke-221"),sQuery(id+"F15.wireOp",EDGE,"E38.sketch_text.stroke-222"),sQuery(id+"F15.wireOp",EDGE,"E38.sketch_text.stroke-223"),sQuery(id+"F15.wireOp",EDGE,"E38.sketch_text.stroke-224"),sQuery(id+"F15.wireOp",EDGE,"E38.sketch_text.stroke-225"),sQuery(id+"F15.wireOp",EDGE,"E38.sketch_text.stroke-226"),sQuery(id+"F15.wireOp",EDGE,"E38.sketch_text.stroke-227"),sQuery(id+"F15.wireOp",EDGE,"E38.sketch_text.stroke-228"),sQuery(id+"F15.wireOp",EDGE,"E38.sketch_text.stroke-229"),sQuery(id+"F15.wireOp",EDGE,"E38.sketch_text.stroke-230"),sQuery(id+"F15.wireOp",EDGE,"E38.sketch_text.stroke-231"),sQuery(id+"F15.wireOp",EDGE,"E38.sketch_text.stroke-232"),sQuery(id+"F15.wireOp",EDGE,"E38.sketch_text.stroke-233")])]});
            var Q12;
            Q12=makeQuery(id+"F16.opExtrude","SWEPT_BODY",BODY,{"disambiguationData":[OSD([sQuery(id+"F15.wireOp",EDGE,"E38.sketch_text.stroke-234"),sQuery(id+"F15.wireOp",EDGE,"E38.sketch_text.stroke-235"),sQuery(id+"F15.wireOp",EDGE,"E38.sketch_text.stroke-236"),sQuery(id+"F15.wireOp",EDGE,"E38.sketch_text.stroke-237"),sQuery(id+"F15.wireOp",EDGE,"E38.sketch_text.stroke-238")])]});
            var Q13;
            Q13=makeQuery(id+"F16.opExtrude","SWEPT_BODY",BODY,{"disambiguationData":[OSD([sQuery(id+"F15.wireOp",EDGE,"E38.sketch_text.stroke-239"),sQuery(id+"F15.wireOp",EDGE,"E38.sketch_text.stroke-240"),sQuery(id+"F15.wireOp",EDGE,"E38.sketch_text.stroke-241"),sQuery(id+"F15.wireOp",EDGE,"E38.sketch_text.stroke-242")])]});
            var Q14;
            Q14=makeQuery(id+"F16.opExtrude","SWEPT_BODY",BODY,{"disambiguationData":[OSD([sQuery(id+"F15.wireOp",EDGE,"E38.sketch_text.stroke-243"),sQuery(id+"F15.wireOp",EDGE,"E38.sketch_text.stroke-244"),sQuery(id+"F15.wireOp",EDGE,"E38.sketch_text.stroke-245"),sQuery(id+"F15.wireOp",EDGE,"E38.sketch_text.stroke-246"),sQuery(id+"F15.wireOp",EDGE,"E38.sketch_text.stroke-247"),sQuery(id+"F15.wireOp",EDGE,"E38.sketch_text.stroke-248"),sQuery(id+"F15.wireOp",EDGE,"E38.sketch_text.stroke-249"),sQuery(id+"F15.wireOp",EDGE,"E38.sketch_text.stroke-250"),sQuery(id+"F15.wireOp",EDGE,"E38.sketch_text.stroke-251"),sQuery(id+"F15.wireOp",EDGE,"E38.sketch_text.stroke-252"),sQuery(id+"F15.wireOp",EDGE,"E38.sketch_text.stroke-253"),sQuery(id+"F15.wireOp",EDGE,"E38.sketch_text.stroke-254"),sQuery(id+"F15.wireOp",EDGE,"E38.sketch_text.stroke-255"),sQuery(id+"F15.wireOp",EDGE,"E38.sketch_text.stroke-256"),sQuery(id+"F15.wireOp",EDGE,"E38.sketch_text.stroke-257"),sQuery(id+"F15.wireOp",EDGE,"E38.sketch_text.stroke-258"),sQuery(id+"F15.wireOp",EDGE,"E38.sketch_text.stroke-259")])]});
            var Q15;
            Q15=makeQuery(id+"F16.opExtrude","SWEPT_BODY",BODY,{"disambiguationData":[OSD([sQuery(id+"F15.wireOp",EDGE,"E38.sketch_text.stroke-260"),sQuery(id+"F15.wireOp",EDGE,"E38.sketch_text.stroke-261"),sQuery(id+"F15.wireOp",EDGE,"E38.sketch_text.stroke-262"),sQuery(id+"F15.wireOp",EDGE,"E38.sketch_text.stroke-263"),sQuery(id+"F15.wireOp",EDGE,"E38.sketch_text.stroke-264"),sQuery(id+"F15.wireOp",EDGE,"E38.sketch_text.stroke-265"),sQuery(id+"F15.wireOp",EDGE,"E38.sketch_text.stroke-266"),sQuery(id+"F15.wireOp",EDGE,"E38.sketch_text.stroke-267"),sQuery(id+"F15.wireOp",EDGE,"E38.sketch_text.stroke-268"),sQuery(id+"F15.wireOp",EDGE,"E38.sketch_text.stroke-269"),sQuery(id+"F15.wireOp",EDGE,"E38.sketch_text.stroke-270"),sQuery(id+"F15.wireOp",EDGE,"E38.sketch_text.stroke-271"),sQuery(id+"F15.wireOp",EDGE,"E38.sketch_text.stroke-272"),sQuery(id+"F15.wireOp",EDGE,"E38.sketch_text.stroke-273"),sQuery(id+"F15.wireOp",EDGE,"E38.sketch_text.stroke-274"),sQuery(id+"F15.wireOp",EDGE,"E38.sketch_text.stroke-275"),sQuery(id+"F15.wireOp",EDGE,"E38.sketch_text.stroke-276"),sQuery(id+"F15.wireOp",EDGE,"E38.sketch_text.stroke-277"),sQuery(id+"F15.wireOp",EDGE,"E38.sketch_text.stroke-278"),sQuery(id+"F15.wireOp",EDGE,"E38.sketch_text.stroke-279")])]});
            var Q16;
            Q16=makeQuery(id+"F16.opExtrude","SWEPT_BODY",BODY,{"disambiguationData":[OSD([sQuery(id+"F15.wireOp",EDGE,"E38.sketch_text.stroke-280"),sQuery(id+"F15.wireOp",EDGE,"E38.sketch_text.stroke-281"),sQuery(id+"F15.wireOp",EDGE,"E38.sketch_text.stroke-282"),sQuery(id+"F15.wireOp",EDGE,"E38.sketch_text.stroke-283"),sQuery(id+"F15.wireOp",EDGE,"E38.sketch_text.stroke-284"),sQuery(id+"F15.wireOp",EDGE,"E38.sketch_text.stroke-285"),sQuery(id+"F15.wireOp",EDGE,"E38.sketch_text.stroke-286"),sQuery(id+"F15.wireOp",EDGE,"E38.sketch_text.stroke-287"),sQuery(id+"F15.wireOp",EDGE,"E38.sketch_text.stroke-288"),sQuery(id+"F15.wireOp",EDGE,"E38.sketch_text.stroke-289"),sQuery(id+"F15.wireOp",EDGE,"E38.sketch_text.stroke-290"),sQuery(id+"F15.wireOp",EDGE,"E38.sketch_text.stroke-291"),sQuery(id+"F15.wireOp",EDGE,"E38.sketch_text.stroke-292"),sQuery(id+"F15.wireOp",EDGE,"E38.sketch_text.stroke-293"),sQuery(id+"F15.wireOp",EDGE,"E38.sketch_text.stroke-294"),sQuery(id+"F15.wireOp",EDGE,"E38.sketch_text.stroke-295"),sQuery(id+"F15.wireOp",EDGE,"E38.sketch_text.stroke-296"),sQuery(id+"F15.wireOp",EDGE,"E38.sketch_text.stroke-297"),sQuery(id+"F15.wireOp",EDGE,"E38.sketch_text.stroke-298"),sQuery(id+"F15.wireOp",EDGE,"E38.sketch_text.stroke-299")])]});
            var Q17;
            Q17=makeQuery(id+"F16.opExtrude","SWEPT_BODY",BODY,{"disambiguationData":[OSD([sQuery(id+"F15.wireOp",EDGE,"E38.sketch_text.stroke-300"),sQuery(id+"F15.wireOp",EDGE,"E38.sketch_text.stroke-301"),sQuery(id+"F15.wireOp",EDGE,"E38.sketch_text.stroke-302"),sQuery(id+"F15.wireOp",EDGE,"E38.sketch_text.stroke-303"),sQuery(id+"F15.wireOp",EDGE,"E38.sketch_text.stroke-304"),sQuery(id+"F15.wireOp",EDGE,"E38.sketch_text.stroke-305"),sQuery(id+"F15.wireOp",EDGE,"E38.sketch_text.stroke-306"),sQuery(id+"F15.wireOp",EDGE,"E38.sketch_text.stroke-307"),sQuery(id+"F15.wireOp",EDGE,"E38.sketch_text.stroke-308"),sQuery(id+"F15.wireOp",EDGE,"E38.sketch_text.stroke-309"),sQuery(id+"F15.wireOp",EDGE,"E38.sketch_text.stroke-310"),sQuery(id+"F15.wireOp",EDGE,"E38.sketch_text.stroke-311"),sQuery(id+"F15.wireOp",EDGE,"E38.sketch_text.stroke-312")])]});
            var Q18;
            Q18=makeQuery(id+"F16.opExtrude","SWEPT_BODY",BODY,{"disambiguationData":[OSD([sQuery(id+"F15.wireOp",EDGE,"E38.sketch_text.stroke-313"),sQuery(id+"F15.wireOp",EDGE,"E38.sketch_text.stroke-314"),sQuery(id+"F15.wireOp",EDGE,"E38.sketch_text.stroke-315"),sQuery(id+"F15.wireOp",EDGE,"E38.sketch_text.stroke-316"),sQuery(id+"F15.wireOp",EDGE,"E38.sketch_text.stroke-317")])]});
            var Q19;
            Q19=makeQuery(id+"F16.opExtrude","SWEPT_BODY",BODY,{"disambiguationData":[OSD([sQuery(id+"F15.wireOp",EDGE,"E38.sketch_text.stroke-318"),sQuery(id+"F15.wireOp",EDGE,"E38.sketch_text.stroke-319"),sQuery(id+"F15.wireOp",EDGE,"E38.sketch_text.stroke-320"),sQuery(id+"F15.wireOp",EDGE,"E38.sketch_text.stroke-321")])]});
            var Q20;
            Q20=makeQuery(id+"F16.opExtrude","SWEPT_BODY",BODY,{"disambiguationData":[OSD([sQuery(id+"F15.wireOp",EDGE,"E38.sketch_text.stroke-322"),sQuery(id+"F15.wireOp",EDGE,"E38.sketch_text.stroke-323"),sQuery(id+"F15.wireOp",EDGE,"E38.sketch_text.stroke-324"),sQuery(id+"F15.wireOp",EDGE,"E38.sketch_text.stroke-325"),sQuery(id+"F15.wireOp",EDGE,"E38.sketch_text.stroke-326"),sQuery(id+"F15.wireOp",EDGE,"E38.sketch_text.stroke-327"),sQuery(id+"F15.wireOp",EDGE,"E38.sketch_text.stroke-328"),sQuery(id+"F15.wireOp",EDGE,"E38.sketch_text.stroke-329"),sQuery(id+"F15.wireOp",EDGE,"E38.sketch_text.stroke-330"),sQuery(id+"F15.wireOp",EDGE,"E38.sketch_text.stroke-331"),sQuery(id+"F15.wireOp",EDGE,"E38.sketch_text.stroke-332"),sQuery(id+"F15.wireOp",EDGE,"E38.sketch_text.stroke-333"),sQuery(id+"F15.wireOp",EDGE,"E38.sketch_text.stroke-334"),sQuery(id+"F15.wireOp",EDGE,"E38.sketch_text.stroke-335"),sQuery(id+"F15.wireOp",EDGE,"E38.sketch_text.stroke-336"),sQuery(id+"F15.wireOp",EDGE,"E38.sketch_text.stroke-337"),sQuery(id+"F15.wireOp",EDGE,"E38.sketch_text.stroke-338")])]});
            var Q21;
            Q21=makeQuery(id+"F16.opExtrude","SWEPT_BODY",BODY,{"disambiguationData":[OSD([sQuery(id+"F15.wireOp",EDGE,"E38.sketch_text.stroke-339"),sQuery(id+"F15.wireOp",EDGE,"E38.sketch_text.stroke-340"),sQuery(id+"F15.wireOp",EDGE,"E38.sketch_text.stroke-341"),sQuery(id+"F15.wireOp",EDGE,"E38.sketch_text.stroke-342"),sQuery(id+"F15.wireOp",EDGE,"E38.sketch_text.stroke-343"),sQuery(id+"F15.wireOp",EDGE,"E38.sketch_text.stroke-344"),sQuery(id+"F15.wireOp",EDGE,"E38.sketch_text.stroke-345"),sQuery(id+"F15.wireOp",EDGE,"E38.sketch_text.stroke-346"),sQuery(id+"F15.wireOp",EDGE,"E38.sketch_text.stroke-347"),sQuery(id+"F15.wireOp",EDGE,"E38.sketch_text.stroke-348"),sQuery(id+"F15.wireOp",EDGE,"E38.sketch_text.stroke-349"),sQuery(id+"F15.wireOp",EDGE,"E38.sketch_text.stroke-350"),sQuery(id+"F15.wireOp",EDGE,"E38.sketch_text.stroke-351"),sQuery(id+"F15.wireOp",EDGE,"E38.sketch_text.stroke-352"),sQuery(id+"F15.wireOp",EDGE,"E38.sketch_text.stroke-353"),sQuery(id+"F15.wireOp",EDGE,"E38.sketch_text.stroke-354"),sQuery(id+"F15.wireOp",EDGE,"E38.sketch_text.stroke-355"),sQuery(id+"F15.wireOp",EDGE,"E38.sketch_text.stroke-356"),sQuery(id+"F15.wireOp",EDGE,"E38.sketch_text.stroke-357"),sQuery(id+"F15.wireOp",EDGE,"E38.sketch_text.stroke-358"),sQuery(id+"F15.wireOp",EDGE,"E38.sketch_text.stroke-359"),sQuery(id+"F15.wireOp",EDGE,"E38.sketch_text.stroke-360"),sQuery(id+"F15.wireOp",EDGE,"E38.sketch_text.stroke-361"),sQuery(id+"F15.wireOp",EDGE,"E38.sketch_text.stroke-362"),sQuery(id+"F15.wireOp",EDGE,"E38.sketch_text.stroke-363"),sQuery(id+"F15.wireOp",EDGE,"E38.sketch_text.stroke-364"),sQuery(id+"F15.wireOp",EDGE,"E38.sketch_text.stroke-365"),sQuery(id+"F15.wireOp",EDGE,"E38.sketch_text.stroke-366"),sQuery(id+"F15.wireOp",EDGE,"E38.sketch_text.stroke-367"),sQuery(id+"F15.wireOp",EDGE,"E38.sketch_text.stroke-368"),sQuery(id+"F15.wireOp",EDGE,"E38.sketch_text.stroke-369"),sQuery(id+"F15.wireOp",EDGE,"E38.sketch_text.stroke-370"),sQuery(id+"F15.wireOp",EDGE,"E38.sketch_text.stroke-371"),sQuery(id+"F15.wireOp",EDGE,"E38.sketch_text.stroke-372"),sQuery(id+"F15.wireOp",EDGE,"E38.sketch_text.stroke-373"),sQuery(id+"F15.wireOp",EDGE,"E38.sketch_text.stroke-374"),sQuery(id+"F15.wireOp",EDGE,"E38.sketch_text.stroke-375"),sQuery(id+"F15.wireOp",EDGE,"E38.sketch_text.stroke-376"),sQuery(id+"F15.wireOp",EDGE,"E38.sketch_text.stroke-377"),sQuery(id+"F15.wireOp",EDGE,"E38.sketch_text.stroke-378"),sQuery(id+"F15.wireOp",EDGE,"E38.sketch_text.stroke-379"),sQuery(id+"F15.wireOp",EDGE,"E38.sketch_text.stroke-380"),sQuery(id+"F15.wireOp",EDGE,"E38.sketch_text.stroke-381"),sQuery(id+"F15.wireOp",EDGE,"E38.sketch_text.stroke-382")])]});
            var Q22;
            Q22=makeQuery(id+"F1.opExtrude","SWEPT_BODY",BODY,{"disambiguationData":[OSD([sQuery(id+"F0.wireOp",EDGE,"E0.bottom"),sQuery(id+"F0.wireOp",EDGE,"E0.top"),sQuery(id+"F0.wireOp",EDGE,"E1"),sQuery(id+"F0.wireOp",EDGE,"E2")])]});
            booleanBodies(context, id + "F23", {"operationType" : BooleanOperationType.SUBTRACTION, "tools" : qUnion([Q0, Q1, Q2, Q3, Q4, Q5, Q6, Q7, Q8, Q9, Q10, Q11, Q12, Q13, Q14, Q15, Q16, Q17, Q18, Q19, Q20, Q21]), "targets" : qUnion([Q22]), "keepTools" : true});
        }
        {
            var Q0;
            Q0=makeQuery(id+"F18.opExtrude","SWEPT_BODY",BODY,{"disambiguationData":[OSD([sQuery(id+"F17.wireOp",EDGE,"E39.sketch_text.stroke-0"),sQuery(id+"F17.wireOp",EDGE,"E39.sketch_text.stroke-1"),sQuery(id+"F17.wireOp",EDGE,"E39.sketch_text.stroke-2"),sQuery(id+"F17.wireOp",EDGE,"E39.sketch_text.stroke-3"),sQuery(id+"F17.wireOp",EDGE,"E39.sketch_text.stroke-4"),sQuery(id+"F17.wireOp",EDGE,"E39.sketch_text.stroke-5"),sQuery(id+"F17.wireOp",EDGE,"E39.sketch_text.stroke-6"),sQuery(id+"F17.wireOp",EDGE,"E39.sketch_text.stroke-7"),sQuery(id+"F17.wireOp",EDGE,"E39.sketch_text.stroke-8"),sQuery(id+"F17.wireOp",EDGE,"E39.sketch_text.stroke-9")])]});
            var Q1;
            Q1=makeQuery(id+"F18.opExtrude","SWEPT_BODY",BODY,{"disambiguationData":[OSD([sQuery(id+"F17.wireOp",EDGE,"E39.sketch_text.stroke-10"),sQuery(id+"F17.wireOp",EDGE,"E39.sketch_text.stroke-11"),sQuery(id+"F17.wireOp",EDGE,"E39.sketch_text.stroke-12"),sQuery(id+"F17.wireOp",EDGE,"E39.sketch_text.stroke-13"),sQuery(id+"F17.wireOp",EDGE,"E39.sketch_text.stroke-14"),sQuery(id+"F17.wireOp",EDGE,"E39.sketch_text.stroke-15"),sQuery(id+"F17.wireOp",EDGE,"E39.sketch_text.stroke-16"),sQuery(id+"F17.wireOp",EDGE,"E39.sketch_text.stroke-17"),sQuery(id+"F17.wireOp",EDGE,"E39.sketch_text.stroke-18"),sQuery(id+"F17.wireOp",EDGE,"E39.sketch_text.stroke-19"),sQuery(id+"F17.wireOp",EDGE,"E39.sketch_text.stroke-20"),sQuery(id+"F17.wireOp",EDGE,"E39.sketch_text.stroke-21"),sQuery(id+"F17.wireOp",EDGE,"E39.sketch_text.stroke-22"),sQuery(id+"F17.wireOp",EDGE,"E39.sketch_text.stroke-23"),sQuery(id+"F17.wireOp",EDGE,"E39.sketch_text.stroke-24"),sQuery(id+"F17.wireOp",EDGE,"E39.sketch_text.stroke-25"),sQuery(id+"F17.wireOp",EDGE,"E39.sketch_text.stroke-26"),sQuery(id+"F17.wireOp",EDGE,"E39.sketch_text.stroke-27"),sQuery(id+"F17.wireOp",EDGE,"E39.sketch_text.stroke-28"),sQuery(id+"F17.wireOp",EDGE,"E39.sketch_text.stroke-29"),sQuery(id+"F17.wireOp",EDGE,"E39.sketch_text.stroke-30"),sQuery(id+"F17.wireOp",EDGE,"E39.sketch_text.stroke-31"),sQuery(id+"F17.wireOp",EDGE,"E39.sketch_text.stroke-32"),sQuery(id+"F17.wireOp",EDGE,"E39.sketch_text.stroke-33"),sQuery(id+"F17.wireOp",EDGE,"E39.sketch_text.stroke-34")])]});
            var Q2;
            Q2=makeQuery(id+"F18.opExtrude","SWEPT_BODY",BODY,{"disambiguationData":[OSD([sQuery(id+"F17.wireOp",EDGE,"E39.sketch_text.stroke-35"),sQuery(id+"F17.wireOp",EDGE,"E39.sketch_text.stroke-36"),sQuery(id+"F17.wireOp",EDGE,"E39.sketch_text.stroke-37"),sQuery(id+"F17.wireOp",EDGE,"E39.sketch_text.stroke-38"),sQuery(id+"F17.wireOp",EDGE,"E39.sketch_text.stroke-39"),sQuery(id+"F17.wireOp",EDGE,"E39.sketch_text.stroke-40"),sQuery(id+"F17.wireOp",EDGE,"E39.sketch_text.stroke-41"),sQuery(id+"F17.wireOp",EDGE,"E39.sketch_text.stroke-42"),sQuery(id+"F17.wireOp",EDGE,"E39.sketch_text.stroke-43"),sQuery(id+"F17.wireOp",EDGE,"E39.sketch_text.stroke-44"),sQuery(id+"F17.wireOp",EDGE,"E39.sketch_text.stroke-45"),sQuery(id+"F17.wireOp",EDGE,"E39.sketch_text.stroke-46"),sQuery(id+"F17.wireOp",EDGE,"E39.sketch_text.stroke-47"),sQuery(id+"F17.wireOp",EDGE,"E39.sketch_text.stroke-48"),sQuery(id+"F17.wireOp",EDGE,"E39.sketch_text.stroke-49"),sQuery(id+"F17.wireOp",EDGE,"E39.sketch_text.stroke-50"),sQuery(id+"F17.wireOp",EDGE,"E39.sketch_text.stroke-51"),sQuery(id+"F17.wireOp",EDGE,"E39.sketch_text.stroke-52"),sQuery(id+"F17.wireOp",EDGE,"E39.sketch_text.stroke-53"),sQuery(id+"F17.wireOp",EDGE,"E39.sketch_text.stroke-54"),sQuery(id+"F17.wireOp",EDGE,"E39.sketch_text.stroke-55"),sQuery(id+"F17.wireOp",EDGE,"E39.sketch_text.stroke-56"),sQuery(id+"F17.wireOp",EDGE,"E39.sketch_text.stroke-57"),sQuery(id+"F17.wireOp",EDGE,"E39.sketch_text.stroke-58"),sQuery(id+"F17.wireOp",EDGE,"E39.sketch_text.stroke-59"),sQuery(id+"F17.wireOp",EDGE,"E39.sketch_text.stroke-60"),sQuery(id+"F17.wireOp",EDGE,"E39.sketch_text.stroke-61")])]});
            var Q3;
            Q3=makeQuery(id+"F18.opExtrude","SWEPT_BODY",BODY,{"disambiguationData":[OSD([sQuery(id+"F17.wireOp",EDGE,"E39.sketch_text.stroke-62"),sQuery(id+"F17.wireOp",EDGE,"E39.sketch_text.stroke-63"),sQuery(id+"F17.wireOp",EDGE,"E39.sketch_text.stroke-64"),sQuery(id+"F17.wireOp",EDGE,"E39.sketch_text.stroke-65"),sQuery(id+"F17.wireOp",EDGE,"E39.sketch_text.stroke-66"),sQuery(id+"F17.wireOp",EDGE,"E39.sketch_text.stroke-67"),sQuery(id+"F17.wireOp",EDGE,"E39.sketch_text.stroke-68"),sQuery(id+"F17.wireOp",EDGE,"E39.sketch_text.stroke-69"),sQuery(id+"F17.wireOp",EDGE,"E39.sketch_text.stroke-70"),sQuery(id+"F17.wireOp",EDGE,"E39.sketch_text.stroke-71")])]});
            var Q4;
            Q4=makeQuery(id+"F18.opExtrude","SWEPT_BODY",BODY,{"disambiguationData":[OSD([sQuery(id+"F17.wireOp",EDGE,"E39.sketch_text.stroke-72"),sQuery(id+"F17.wireOp",EDGE,"E39.sketch_text.stroke-73"),sQuery(id+"F17.wireOp",EDGE,"E39.sketch_text.stroke-74"),sQuery(id+"F17.wireOp",EDGE,"E39.sketch_text.stroke-75"),sQuery(id+"F17.wireOp",EDGE,"E39.sketch_text.stroke-76"),sQuery(id+"F17.wireOp",EDGE,"E39.sketch_text.stroke-77"),sQuery(id+"F17.wireOp",EDGE,"E39.sketch_text.stroke-78"),sQuery(id+"F17.wireOp",EDGE,"E39.sketch_text.stroke-79"),sQuery(id+"F17.wireOp",EDGE,"E39.sketch_text.stroke-80"),sQuery(id+"F17.wireOp",EDGE,"E39.sketch_text.stroke-81")])]});
            var Q5;
            Q5=makeQuery(id+"F18.opExtrude","SWEPT_BODY",BODY,{"disambiguationData":[OSD([sQuery(id+"F17.wireOp",EDGE,"E39.sketch_text.stroke-82"),sQuery(id+"F17.wireOp",EDGE,"E39.sketch_text.stroke-83"),sQuery(id+"F17.wireOp",EDGE,"E39.sketch_text.stroke-84"),sQuery(id+"F17.wireOp",EDGE,"E39.sketch_text.stroke-85"),sQuery(id+"F17.wireOp",EDGE,"E39.sketch_text.stroke-86"),sQuery(id+"F17.wireOp",EDGE,"E39.sketch_text.stroke-87"),sQuery(id+"F17.wireOp",EDGE,"E39.sketch_text.stroke-88"),sQuery(id+"F17.wireOp",EDGE,"E39.sketch_text.stroke-89"),sQuery(id+"F17.wireOp",EDGE,"E39.sketch_text.stroke-90"),sQuery(id+"F17.wireOp",EDGE,"E39.sketch_text.stroke-91"),sQuery(id+"F17.wireOp",EDGE,"E39.sketch_text.stroke-92"),sQuery(id+"F17.wireOp",EDGE,"E39.sketch_text.stroke-93"),sQuery(id+"F17.wireOp",EDGE,"E39.sketch_text.stroke-94"),sQuery(id+"F17.wireOp",EDGE,"E39.sketch_text.stroke-95"),sQuery(id+"F17.wireOp",EDGE,"E39.sketch_text.stroke-96"),sQuery(id+"F17.wireOp",EDGE,"E39.sketch_text.stroke-97"),sQuery(id+"F17.wireOp",EDGE,"E39.sketch_text.stroke-98"),sQuery(id+"F17.wireOp",EDGE,"E39.sketch_text.stroke-99"),sQuery(id+"F17.wireOp",EDGE,"E39.sketch_text.stroke-100"),sQuery(id+"F17.wireOp",EDGE,"E39.sketch_text.stroke-101"),sQuery(id+"F17.wireOp",EDGE,"E39.sketch_text.stroke-102"),sQuery(id+"F17.wireOp",EDGE,"E39.sketch_text.stroke-103"),sQuery(id+"F17.wireOp",EDGE,"E39.sketch_text.stroke-104"),sQuery(id+"F17.wireOp",EDGE,"E39.sketch_text.stroke-105"),sQuery(id+"F17.wireOp",EDGE,"E39.sketch_text.stroke-106"),sQuery(id+"F17.wireOp",EDGE,"E39.sketch_text.stroke-107"),sQuery(id+"F17.wireOp",EDGE,"E39.sketch_text.stroke-108")])]});
            var Q6;
            Q6=makeQuery(id+"F18.opExtrude","SWEPT_BODY",BODY,{"disambiguationData":[OSD([sQuery(id+"F17.wireOp",EDGE,"E39.sketch_text.stroke-109"),sQuery(id+"F17.wireOp",EDGE,"E39.sketch_text.stroke-110"),sQuery(id+"F17.wireOp",EDGE,"E39.sketch_text.stroke-111"),sQuery(id+"F17.wireOp",EDGE,"E39.sketch_text.stroke-112"),sQuery(id+"F17.wireOp",EDGE,"E39.sketch_text.stroke-113"),sQuery(id+"F17.wireOp",EDGE,"E39.sketch_text.stroke-114"),sQuery(id+"F17.wireOp",EDGE,"E39.sketch_text.stroke-115"),sQuery(id+"F17.wireOp",EDGE,"E39.sketch_text.stroke-116"),sQuery(id+"F17.wireOp",EDGE,"E39.sketch_text.stroke-117"),sQuery(id+"F17.wireOp",EDGE,"E39.sketch_text.stroke-118"),sQuery(id+"F17.wireOp",EDGE,"E39.sketch_text.stroke-119"),sQuery(id+"F17.wireOp",EDGE,"E39.sketch_text.stroke-120"),sQuery(id+"F17.wireOp",EDGE,"E39.sketch_text.stroke-121"),sQuery(id+"F17.wireOp",EDGE,"E39.sketch_text.stroke-122"),sQuery(id+"F17.wireOp",EDGE,"E39.sketch_text.stroke-123"),sQuery(id+"F17.wireOp",EDGE,"E39.sketch_text.stroke-124"),sQuery(id+"F17.wireOp",EDGE,"E39.sketch_text.stroke-125"),sQuery(id+"F17.wireOp",EDGE,"E39.sketch_text.stroke-126"),sQuery(id+"F17.wireOp",EDGE,"E39.sketch_text.stroke-127"),sQuery(id+"F17.wireOp",EDGE,"E39.sketch_text.stroke-128"),sQuery(id+"F17.wireOp",EDGE,"E39.sketch_text.stroke-129"),sQuery(id+"F17.wireOp",EDGE,"E39.sketch_text.stroke-130"),sQuery(id+"F17.wireOp",EDGE,"E39.sketch_text.stroke-131"),sQuery(id+"F17.wireOp",EDGE,"E39.sketch_text.stroke-132"),sQuery(id+"F17.wireOp",EDGE,"E39.sketch_text.stroke-133")])]});
            var Q7;
            Q7=makeQuery(id+"F18.opExtrude","SWEPT_BODY",BODY,{"disambiguationData":[OSD([sQuery(id+"F17.wireOp",EDGE,"E39.sketch_text.stroke-134"),sQuery(id+"F17.wireOp",EDGE,"E39.sketch_text.stroke-135"),sQuery(id+"F17.wireOp",EDGE,"E39.sketch_text.stroke-136"),sQuery(id+"F17.wireOp",EDGE,"E39.sketch_text.stroke-137"),sQuery(id+"F17.wireOp",EDGE,"E39.sketch_text.stroke-138"),sQuery(id+"F17.wireOp",EDGE,"E39.sketch_text.stroke-139"),sQuery(id+"F17.wireOp",EDGE,"E39.sketch_text.stroke-140"),sQuery(id+"F17.wireOp",EDGE,"E39.sketch_text.stroke-141"),sQuery(id+"F17.wireOp",EDGE,"E39.sketch_text.stroke-142"),sQuery(id+"F17.wireOp",EDGE,"E39.sketch_text.stroke-143"),sQuery(id+"F17.wireOp",EDGE,"E39.sketch_text.stroke-144"),sQuery(id+"F17.wireOp",EDGE,"E39.sketch_text.stroke-145"),sQuery(id+"F17.wireOp",EDGE,"E39.sketch_text.stroke-146"),sQuery(id+"F17.wireOp",EDGE,"E39.sketch_text.stroke-147"),sQuery(id+"F17.wireOp",EDGE,"E39.sketch_text.stroke-148"),sQuery(id+"F17.wireOp",EDGE,"E39.sketch_text.stroke-149")])]});
            var Q8;
            Q8=makeQuery(id+"F18.opExtrude","SWEPT_BODY",BODY,{"disambiguationData":[OSD([sQuery(id+"F17.wireOp",EDGE,"E39.sketch_text.stroke-150"),sQuery(id+"F17.wireOp",EDGE,"E39.sketch_text.stroke-151"),sQuery(id+"F17.wireOp",EDGE,"E39.sketch_text.stroke-152"),sQuery(id+"F17.wireOp",EDGE,"E39.sketch_text.stroke-153")])]});
            var Q9;
            Q9=makeQuery(id+"F18.opExtrude","SWEPT_BODY",BODY,{"disambiguationData":[OSD([sQuery(id+"F17.wireOp",EDGE,"E39.sketch_text.stroke-154"),sQuery(id+"F17.wireOp",EDGE,"E39.sketch_text.stroke-155"),sQuery(id+"F17.wireOp",EDGE,"E39.sketch_text.stroke-156"),sQuery(id+"F17.wireOp",EDGE,"E39.sketch_text.stroke-157"),sQuery(id+"F17.wireOp",EDGE,"E39.sketch_text.stroke-158"),sQuery(id+"F17.wireOp",EDGE,"E39.sketch_text.stroke-159"),sQuery(id+"F17.wireOp",EDGE,"E39.sketch_text.stroke-160"),sQuery(id+"F17.wireOp",EDGE,"E39.sketch_text.stroke-161"),sQuery(id+"F17.wireOp",EDGE,"E39.sketch_text.stroke-162"),sQuery(id+"F17.wireOp",EDGE,"E39.sketch_text.stroke-163")])]});
            var Q10;
            Q10=makeQuery(id+"F18.opExtrude","SWEPT_BODY",BODY,{"disambiguationData":[OSD([sQuery(id+"F17.wireOp",EDGE,"E39.sketch_text.stroke-164"),sQuery(id+"F17.wireOp",EDGE,"E39.sketch_text.stroke-165"),sQuery(id+"F17.wireOp",EDGE,"E39.sketch_text.stroke-166"),sQuery(id+"F17.wireOp",EDGE,"E39.sketch_text.stroke-167"),sQuery(id+"F17.wireOp",EDGE,"E39.sketch_text.stroke-168"),sQuery(id+"F17.wireOp",EDGE,"E39.sketch_text.stroke-169"),sQuery(id+"F17.wireOp",EDGE,"E39.sketch_text.stroke-170"),sQuery(id+"F17.wireOp",EDGE,"E39.sketch_text.stroke-171"),sQuery(id+"F17.wireOp",EDGE,"E39.sketch_text.stroke-172"),sQuery(id+"F17.wireOp",EDGE,"E39.sketch_text.stroke-173"),sQuery(id+"F17.wireOp",EDGE,"E39.sketch_text.stroke-174"),sQuery(id+"F17.wireOp",EDGE,"E39.sketch_text.stroke-175"),sQuery(id+"F17.wireOp",EDGE,"E39.sketch_text.stroke-176"),sQuery(id+"F17.wireOp",EDGE,"E39.sketch_text.stroke-177"),sQuery(id+"F17.wireOp",EDGE,"E39.sketch_text.stroke-178"),sQuery(id+"F17.wireOp",EDGE,"E39.sketch_text.stroke-179"),sQuery(id+"F17.wireOp",EDGE,"E39.sketch_text.stroke-180"),sQuery(id+"F17.wireOp",EDGE,"E39.sketch_text.stroke-181"),sQuery(id+"F17.wireOp",EDGE,"E39.sketch_text.stroke-182"),sQuery(id+"F17.wireOp",EDGE,"E39.sketch_text.stroke-183"),sQuery(id+"F17.wireOp",EDGE,"E39.sketch_text.stroke-184"),sQuery(id+"F17.wireOp",EDGE,"E39.sketch_text.stroke-185"),sQuery(id+"F17.wireOp",EDGE,"E39.sketch_text.stroke-186"),sQuery(id+"F17.wireOp",EDGE,"E39.sketch_text.stroke-187")])]});
            var Q11;
            Q11=makeQuery(id+"F18.opExtrude","SWEPT_BODY",BODY,{"disambiguationData":[OSD([sQuery(id+"F17.wireOp",EDGE,"E39.sketch_text.stroke-188"),sQuery(id+"F17.wireOp",EDGE,"E39.sketch_text.stroke-189"),sQuery(id+"F17.wireOp",EDGE,"E39.sketch_text.stroke-190"),sQuery(id+"F17.wireOp",EDGE,"E39.sketch_text.stroke-191"),sQuery(id+"F17.wireOp",EDGE,"E39.sketch_text.stroke-192"),sQuery(id+"F17.wireOp",EDGE,"E39.sketch_text.stroke-193"),sQuery(id+"F17.wireOp",EDGE,"E39.sketch_text.stroke-194"),sQuery(id+"F17.wireOp",EDGE,"E39.sketch_text.stroke-195"),sQuery(id+"F17.wireOp",EDGE,"E39.sketch_text.stroke-196"),sQuery(id+"F17.wireOp",EDGE,"E39.sketch_text.stroke-197"),sQuery(id+"F17.wireOp",EDGE,"E39.sketch_text.stroke-198"),sQuery(id+"F17.wireOp",EDGE,"E39.sketch_text.stroke-199"),sQuery(id+"F17.wireOp",EDGE,"E39.sketch_text.stroke-200"),sQuery(id+"F17.wireOp",EDGE,"E39.sketch_text.stroke-201"),sQuery(id+"F17.wireOp",EDGE,"E39.sketch_text.stroke-202"),sQuery(id+"F17.wireOp",EDGE,"E39.sketch_text.stroke-203")])]});
            var Q12;
            Q12=makeQuery(id+"F18.opExtrude","SWEPT_BODY",BODY,{"disambiguationData":[OSD([sQuery(id+"F17.wireOp",EDGE,"E39.sketch_text.stroke-204"),sQuery(id+"F17.wireOp",EDGE,"E39.sketch_text.stroke-205"),sQuery(id+"F17.wireOp",EDGE,"E39.sketch_text.stroke-206"),sQuery(id+"F17.wireOp",EDGE,"E39.sketch_text.stroke-207"),sQuery(id+"F17.wireOp",EDGE,"E39.sketch_text.stroke-208"),sQuery(id+"F17.wireOp",EDGE,"E39.sketch_text.stroke-209"),sQuery(id+"F17.wireOp",EDGE,"E39.sketch_text.stroke-210"),sQuery(id+"F17.wireOp",EDGE,"E39.sketch_text.stroke-211"),sQuery(id+"F17.wireOp",EDGE,"E39.sketch_text.stroke-212"),sQuery(id+"F17.wireOp",EDGE,"E39.sketch_text.stroke-213"),sQuery(id+"F17.wireOp",EDGE,"E39.sketch_text.stroke-214"),sQuery(id+"F17.wireOp",EDGE,"E39.sketch_text.stroke-215"),sQuery(id+"F17.wireOp",EDGE,"E39.sketch_text.stroke-216"),sQuery(id+"F17.wireOp",EDGE,"E39.sketch_text.stroke-217"),sQuery(id+"F17.wireOp",EDGE,"E39.sketch_text.stroke-218"),sQuery(id+"F17.wireOp",EDGE,"E39.sketch_text.stroke-219"),sQuery(id+"F17.wireOp",EDGE,"E39.sketch_text.stroke-220"),sQuery(id+"F17.wireOp",EDGE,"E39.sketch_text.stroke-221"),sQuery(id+"F17.wireOp",EDGE,"E39.sketch_text.stroke-222"),sQuery(id+"F17.wireOp",EDGE,"E39.sketch_text.stroke-223"),sQuery(id+"F17.wireOp",EDGE,"E39.sketch_text.stroke-224"),sQuery(id+"F17.wireOp",EDGE,"E39.sketch_text.stroke-225"),sQuery(id+"F17.wireOp",EDGE,"E39.sketch_text.stroke-226"),sQuery(id+"F17.wireOp",EDGE,"E39.sketch_text.stroke-227"),sQuery(id+"F17.wireOp",EDGE,"E39.sketch_text.stroke-228"),sQuery(id+"F17.wireOp",EDGE,"E39.sketch_text.stroke-229"),sQuery(id+"F17.wireOp",EDGE,"E39.sketch_text.stroke-230"),sQuery(id+"F17.wireOp",EDGE,"E39.sketch_text.stroke-231"),sQuery(id+"F17.wireOp",EDGE,"E39.sketch_text.stroke-232"),sQuery(id+"F17.wireOp",EDGE,"E39.sketch_text.stroke-233"),sQuery(id+"F17.wireOp",EDGE,"E39.sketch_text.stroke-234")])]});
            var Q13;
            Q13=makeQuery(id+"F1.opExtrude","SWEPT_BODY",BODY,{"disambiguationData":[OSD([sQuery(id+"F0.wireOp",EDGE,"E0.bottom"),sQuery(id+"F0.wireOp",EDGE,"E0.top"),sQuery(id+"F0.wireOp",EDGE,"E1"),sQuery(id+"F0.wireOp",EDGE,"E2")])]});
            booleanBodies(context, id + "F24", {"operationType" : BooleanOperationType.SUBTRACTION, "tools" : qUnion([Q0, Q1, Q2, Q3, Q4, Q5, Q6, Q7, Q8, Q9, Q10, Q11, Q12]), "targets" : qUnion([Q13]), "keepTools" : true});
        }
        {
            var Q0;
            Q0=makeQuery(id+"F12.opExtrude","SWEPT_BODY",BODY,{"disambiguationData":[OSD([sQuery(id+"F11.wireOp",EDGE,"E36.1.0")])]});
            var Q1;
            Q1=makeQuery(id+"F1.opExtrude","SWEPT_BODY",BODY,{"disambiguationData":[OSD([sQuery(id+"F0.wireOp",EDGE,"E0.bottom"),sQuery(id+"F0.wireOp",EDGE,"E0.top"),sQuery(id+"F0.wireOp",EDGE,"E1"),sQuery(id+"F0.wireOp",EDGE,"E2")])]});
            booleanBodies(context, id + "F25", {"operationType" : BooleanOperationType.SUBTRACTION, "tools" : qUnion([Q0]), "targets" : qUnion([Q1]), "keepTools" : true});
        }
        {
            var Q0;
            Q0=qCreatedBy(makeId("Top.planeOp"),FACE);
            var sketch = newSketch(context, id + "F26", { "sketchPlane" : qUnion([Q0])});
            skCircle(sketch, "E40", {"center": v(-48, 0) * mm, "radius": 1.63 * mm});
            skCircle(sketch, "E41.MirrorC", {"center": v(48, 0) * mm, "radius": 1.63 * mm});
            skSolve(sketch);
        }
        {
            var Q0;
            Q0 = qSketchRegion(id + "F26", true);
            extrude(context, id + "F27", {"entities" : qUnion([Q0]), "operationType" : NewBodyOperationType.REMOVE, "endBound" : BoundingType.THROUGH_ALL, "depth" : 25 * mm});
        }
    });
